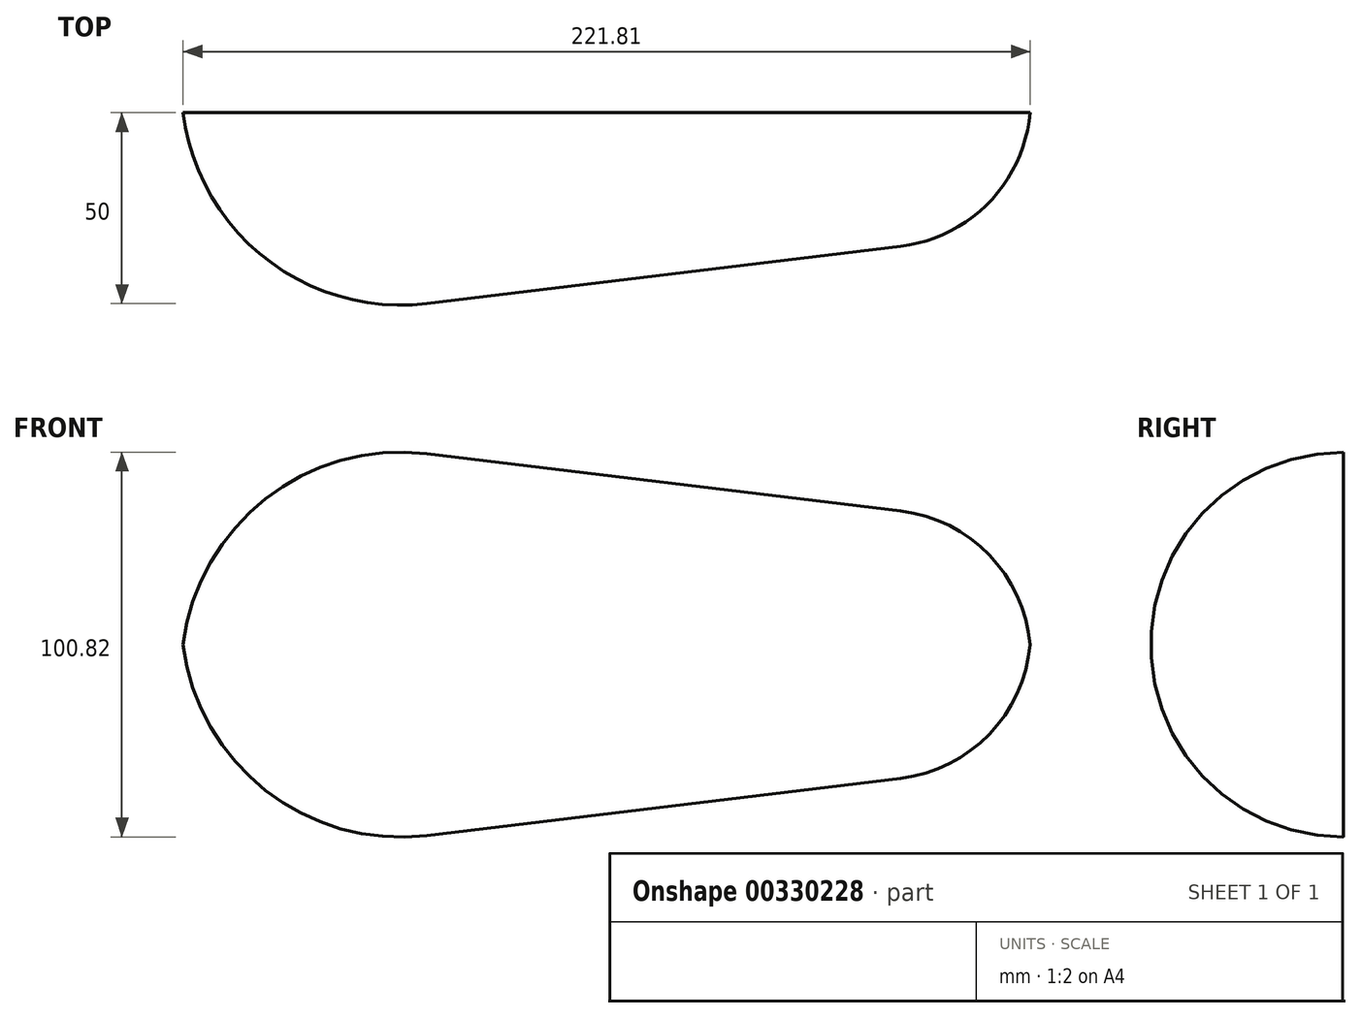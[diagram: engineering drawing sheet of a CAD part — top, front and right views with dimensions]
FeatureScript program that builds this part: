
annotation { "Feature Type Name" : "Feature", "Feature Type Description" : "" }
export const myFeature = defineFeature(function(context is Context, id is Id, definition is map)
    precondition{}
    {
        {
            var Q0;
            Q0=qCreatedBy(makeId("Front.planeOp"),FACE);
            var sketch = newSketch(context, id + "F0", { "sketchPlane" : qUnion([Q0])});
            skLineSegment(sketch, "E0", {"start": v(-28.98, 50) * mm, "end": v(95.12, 35) * mm});
            skLineSegment(sketch, "E1", {"start": v(-156.53, 0) * mm, "end": v(139.7, 0) * mm, "construction": true});
            skArc(sketch, "E2", {"start": v(-28.98, 50) * mm, "mid": v(-71.26, 38.21) * mm, "end": v(-92.85, 0) * mm});
            skArc(sketch, "E3", {"start": v(95.12, 35) * mm, "mid": v(118.25, 23.5) * mm, "end": v(128.96, 0) * mm});
            skArc(sketch, "E4.0", {"start": v(94.74, 31.92) * mm, "mid": v(116.02, 21.35) * mm, "end": v(125.87, -0.27) * mm});
            skLineSegment(sketch, "E4.1", {"start": v(-29.35, 46.92) * mm, "end": v(94.74, 31.92) * mm});
            skArc(sketch, "E4.2", {"start": v(-29.35, 46.92) * mm, "mid": v(-69.35, 35.77) * mm, "end": v(-89.78, -0.38) * mm});
            skSolve(sketch);
        }
        {
            var Q0;
            Q0=sQuery(id+"F0.wireOp",EDGE,"E1");
            var Q1;
            Q1=sQuery(id+"F0.wireOp",EDGE,"E2");
            var Q2;
            Q2=sQuery(id+"F0.wireOp",EDGE,"E0");
            var Q3;
            Q3=sQuery(id+"F0.wireOp",EDGE,"E3");
            var Q4;
            Q4=sQuery(id+"F0.wireOp",EDGE,"E1");
            revolve(context, id + "F1", {"bodyType" : ToolBodyType.SURFACE, "surfaceEntities" : qUnion([Q0, Q1, Q2, Q3]), "axis" : qUnion([Q4]), "revolveType" : RevolveType.ONE_DIRECTION, "angle" : 180 * degree});
        }
    });
